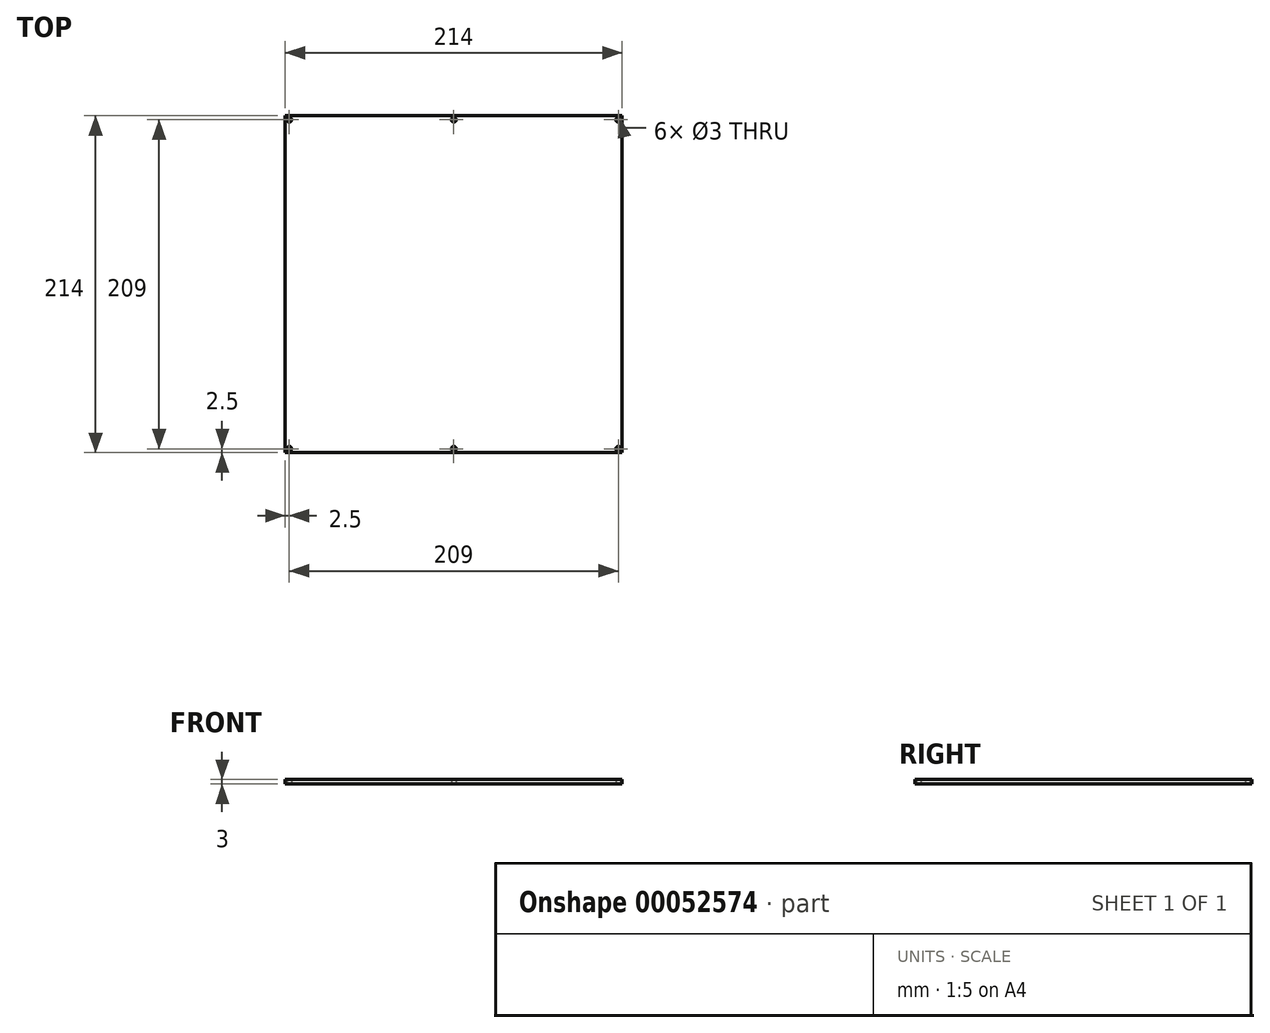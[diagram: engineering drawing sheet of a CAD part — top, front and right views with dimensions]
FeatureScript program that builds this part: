
annotation { "Feature Type Name" : "Feature", "Feature Type Description" : "" }
export const myFeature = defineFeature(function(context is Context, id is Id, definition is map)
    precondition{}
    {
        {
            var Q0;
            Q0=qCreatedBy(makeId("Top.planeOp"),FACE);
            var sketch = newSketch(context, id + "F0", { "sketchPlane" : qUnion([Q0])});
            skLineSegment(sketch, "E0", {"start": v(0, 0) * mm, "end": v(-107, 107) * mm, "construction": true});
            skCircle(sketch, "E1", {"center": v(-104.5, 104.5) * mm, "radius": 1.5 * mm});
            skLineSegment(sketch, "E2.MirrorCS", {"start": v(0, 0) * mm, "end": v(107, 107) * mm, "construction": true});
            skCircle(sketch, "E3.MirrorC", {"center": v(104.5, 104.5) * mm, "radius": 1.5 * mm});
            skCircle(sketch, "E4.MirrorC", {"center": v(-104.5, -104.5) * mm, "radius": 1.5 * mm});
            skLineSegment(sketch, "E5.MirrorCS", {"start": v(0, 0) * mm, "end": v(-107, -107) * mm, "construction": true});
            skCircle(sketch, "E6.MirrorC", {"center": v(104.5, -104.5) * mm, "radius": 1.5 * mm});
            skLineSegment(sketch, "E7.MirrorCS", {"start": v(0, 0) * mm, "end": v(107, -107) * mm, "construction": true});
            skLineSegment(sketch, "E8", {"start": v(-107, -107) * mm, "end": v(107, -107) * mm});
            skLineSegment(sketch, "E9", {"start": v(107, -107) * mm, "end": v(107, 107) * mm});
            skLineSegment(sketch, "E10", {"start": v(107, 107) * mm, "end": v(-107, 107) * mm});
            skLineSegment(sketch, "E11", {"start": v(-107, 107) * mm, "end": v(-107, -107) * mm});
            skCircle(sketch, "E12", {"center": v(0, -104.5) * mm, "radius": 1.5 * mm});
            skCircle(sketch, "E13.MirrorC", {"center": v(0, 104.5) * mm, "radius": 1.5 * mm});
            skSolve(sketch);
        }
        {
            var Q0;
            Q0=qSketchRegion(id+"F0",true);
            extrude(context, id + "F1", {"entities" : qUnion([Q0]), "depth" : 3 * mm});
        }
    });
